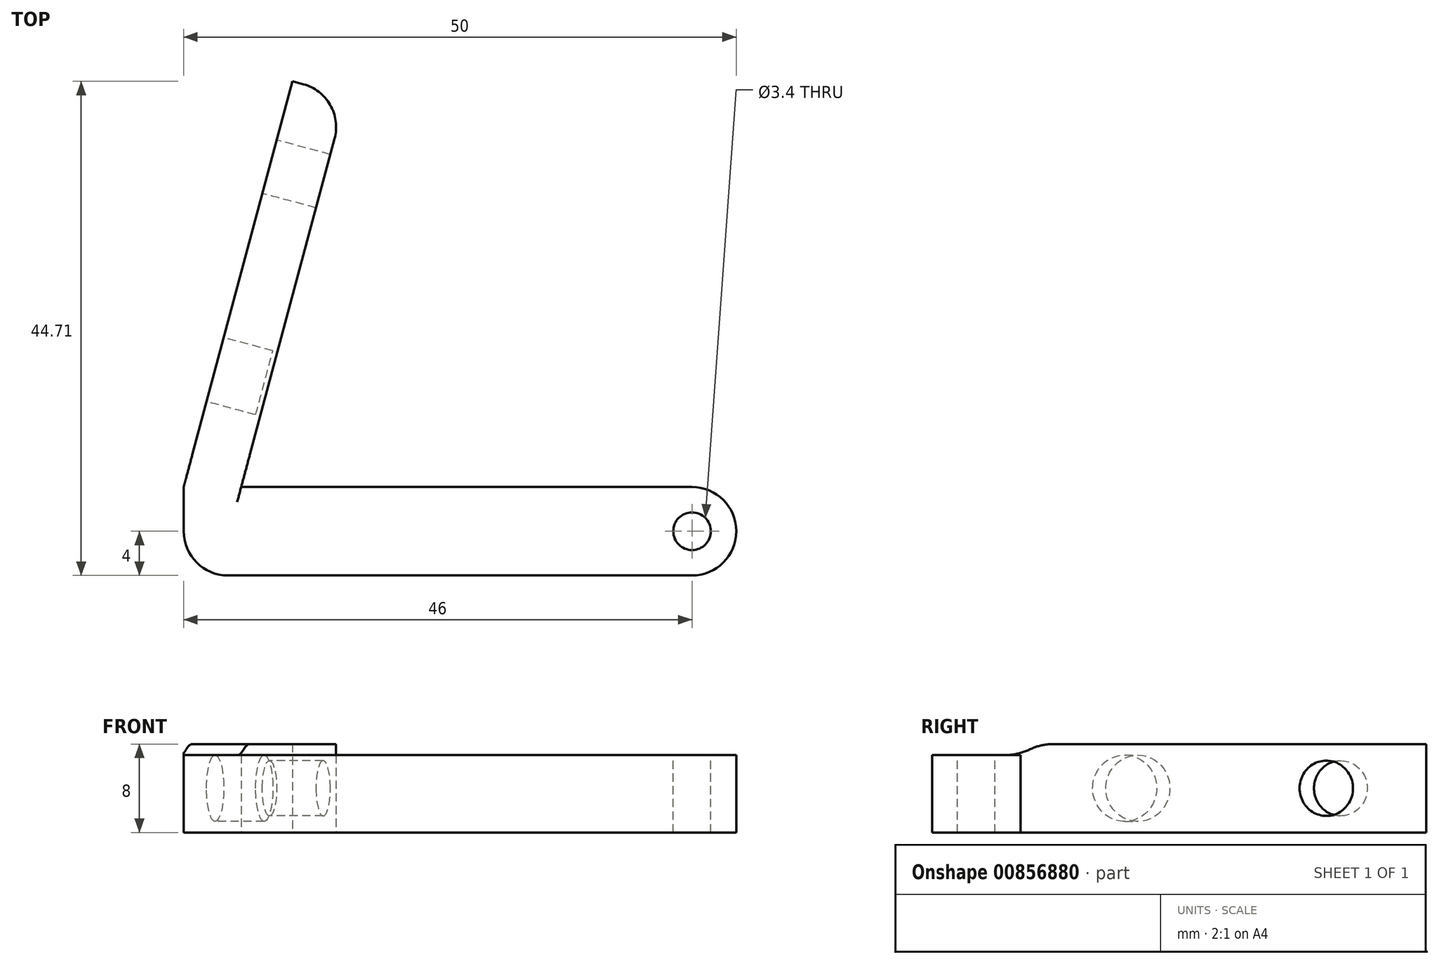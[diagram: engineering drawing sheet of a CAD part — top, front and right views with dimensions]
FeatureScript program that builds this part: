
annotation { "Feature Type Name" : "Feature", "Feature Type Description" : "" }
export const myFeature = defineFeature(function(context is Context, id is Id, definition is map)
    precondition{}
    {
        {
            var Q0;
            Q0=qCreatedBy(makeId("Top.planeOp"),FACE);
            var sketch = newSketch(context, id + "F0", { "sketchPlane" : qUnion([Q0])});
            skLineSegment(sketch, "E0.bottom", {"start": v(25, -4) * mm, "end": v(-25, -4) * mm});
            skLineSegment(sketch, "E0.top", {"start": v(25, 4) * mm, "end": v(-25, 4) * mm});
            skLineSegment(sketch, "E0.left", {"start": v(25, -4) * mm, "end": v(25, 4) * mm});
            skLineSegment(sketch, "E0.right", {"start": v(-25, -4) * mm, "end": v(-25, 4) * mm});
            skPoint(sketch, "E0.middle", {"position": v(0, 0) * mm});
            skLineSegment(sketch, "E1", {"start": v(-25, 4) * mm, "end": v(-15.16, 40.7) * mm});
            skLineSegment(sketch, "E2", {"start": v(-15.16, 40.7) * mm, "end": v(-10.31, 39.4) * mm});
            skLineSegment(sketch, "E3", {"start": v(-10.31, 39.4) * mm, "end": v(-19.8, 4) * mm});
            skSolve(sketch);
        }
        {
            var Q0;
            Q0=makeQuery(id+"F0.imprint","IMPRINT",FACE,{"disambiguationData":[TD([[makeQuery(id+"F0.imprint","IMPRINT",EDGE,{"derivedFrom":sQuery(id+"F0.wireOp",EDGE,"E0.bottom")}),-1.0]])]});
            extrude(context, id + "F1", {"entities" : qUnion([Q0]), "depth" : 7 * mm, "offsetDistance" : 25 * mm});
        }
        {
            var Q0;
            {var subQ0=sQuery(id+"F0.wireOp",EDGE,"E1");Q0=makeQuery(id+"F0.imprint","IMPRINT",FACE,{"disambiguationData":[TD([[makeQuery(id+"F0.imprint","IMPRINT",EDGE,{"derivedFrom":subQ0}),-1.0]])]});}
            extrude(context, id + "F2", {"entities" : qUnion([Q0]), "operationType" : NewBodyOperationType.ADD, "depth" : 8 * mm, "offsetDistance" : 25 * mm});
        }
        {
            var Q0;
            Q0=makeQuery(id+"F1.opExtrude","SWEPT_EDGE",EDGE,{"disambiguationData":[OSD([sQuery(id+"F0.wireOp",EDGE,"E0.top"),sQuery(id+"F0.wireOp",EDGE,"E0.left")])]});
            var Q1;
            Q1=makeQuery(id+"F1.opExtrude","SWEPT_EDGE",EDGE,{"disambiguationData":[OSD([sQuery(id+"F0.wireOp",EDGE,"E0.bottom"),sQuery(id+"F0.wireOp",EDGE,"E0.left")])]});
            var Q2;
            Q2=makeQuery(id+"F1.opExtrude","SWEPT_EDGE",EDGE,{"disambiguationData":[OSD([sQuery(id+"F0.wireOp",EDGE,"E0.bottom"),sQuery(id+"F0.wireOp",EDGE,"E0.right")])]});
            var Q3;
            Q3=makeQuery(id+"F2.opExtrude","SWEPT_EDGE",EDGE,{"disambiguationData":[OSD([sQuery(id+"F0.wireOp",EDGE,"E2"),sQuery(id+"F0.wireOp",EDGE,"E3")])]});
            fillet(context, id + "F3", {"entities" : qUnion([Q0, Q1, Q2, Q3]), "radius" : 4 * mm, "tangentPropagation" : true, "allowEdgeOverflow" : false});
        }
        {
            var Q0;
            Q0=makeQuery(id+"F2.opExtrude","CAP_EDGE",EDGE,{"disambiguationData":[OSD([sQuery(id+"F0.wireOp",EDGE,"E0.top")])],"isStart":false});
            fillet(context, id + "F4", {"entities" : qUnion([Q0]), "radius" : 5 * mm, "tangentPropagation" : true, "allowEdgeOverflow" : false});
        }
        {
            var Q0;
            {var subQ0=sQuery(id+"F0.wireOp",EDGE,"E0.top");Q0=makeQuery(id+"F4.opFillet","BLEND_EDGE",EDGE,{"blendedFrom":[makeQuery(id+"F2.opExtrude","CAP_EDGE",EDGE,{"disambiguationData":[OSD([subQ0])],"isStart":false}),makeQuery(id+"F1.opExtrude","CAP_FACE",FACE,{"disambiguationData":[OSD([sQuery(id+"F0.wireOp",EDGE,"E0.bottom"),subQ0,sQuery(id+"F0.wireOp",EDGE,"E0.left"),sQuery(id+"F0.wireOp",EDGE,"E0.right")])],"isStart":false})],"blendedInto":[makeQuery(id+"F1.opExtrude","CAP_FACE",FACE,{"disambiguationData":[OSD([sQuery(id+"F0.wireOp",EDGE,"E0.bottom"),subQ0,sQuery(id+"F0.wireOp",EDGE,"E0.left"),sQuery(id+"F0.wireOp",EDGE,"E0.right")])],"isStart":false})]});}
            fillet(context, id + "F5", {"entities" : qUnion([Q0]), "radius" : 5 * mm, "tangentPropagation" : true, "allowEdgeOverflow" : false});
        }
        {
            var Q0;
            Q0=makeQuery(id+"F2.opExtrude","SWEPT_FACE",FACE,{"disambiguationData":[OSD([sQuery(id+"F0.wireOp",EDGE,"E1")])]});
            var sketch = newSketch(context, id + "F6", { "sketchPlane" : qUnion([Q0])});
            skCircle(sketch, "E4", {"center": v(-27.4, 4) * mm, "radius": 2.5 * mm});
            skPoint(sketch, "E4.centerSnap0", {"position": v(-35.4, 4) * mm});
            skCircle(sketch, "E5", {"center": v(-8.4, 4) * mm, "radius": 3 * mm});
            skSolve(sketch);
        }
        {
            var Q0;
            Q0=makeQuery(id+"F6.imprint","IMPRINT",FACE,{"disambiguationData":[TD([[makeQuery(id+"F6.imprint","IMPRINT",EDGE,{"derivedFrom":sQuery(id+"F6.wireOp",EDGE,"E4")}),1.0]])]});
            extrude(context, id + "F7", {"entities" : qUnion([Q0]), "operationType" : NewBodyOperationType.REMOVE, "oppositeDirection" : true, "depth" : 10 * mm, "offsetDistance" : 25 * mm});
        }
        {
            var Q0;
            Q0=makeQuery(id+"F6.imprint","IMPRINT",FACE,{"disambiguationData":[TD([[makeQuery(id+"F6.imprint","IMPRINT",EDGE,{"derivedFrom":sQuery(id+"F6.wireOp",EDGE,"E5")}),1.0]])]});
            extrude(context, id + "F8", {"entities" : qUnion([Q0]), "operationType" : NewBodyOperationType.REMOVE, "oppositeDirection" : true, "depth" : 4.6 * mm, "offsetDistance" : 25 * mm});
        }
        {
            var Q0;
            Q0=makeQuery(id+"F1.opExtrude","CAP_FACE",FACE,{"disambiguationData":[OSD([sQuery(id+"F0.wireOp",EDGE,"E0.bottom"),sQuery(id+"F0.wireOp",EDGE,"E0.top"),sQuery(id+"F0.wireOp",EDGE,"E0.left"),sQuery(id+"F0.wireOp",EDGE,"E0.right")])],"isStart":false});
            var sketch = newSketch(context, id + "F9", { "sketchPlane" : qUnion([Q0])});
            skCircle(sketch, "E6", {"center": v(21, 0) * mm, "radius": 1.7 * mm});
            skSolve(sketch);
        }
        {
            var Q0;
            Q0=makeQuery(id+"F9.imprint","IMPRINT",FACE,{"disambiguationData":[TD([[makeQuery(id+"F9.imprint","IMPRINT",EDGE,{"derivedFrom":sQuery(id+"F9.wireOp",EDGE,"E6")}),1.0]])]});
            extrude(context, id + "F10", {"entities" : qUnion([Q0]), "operationType" : NewBodyOperationType.REMOVE, "endBound" : BoundingType.THROUGH_ALL, "oppositeDirection" : true, "depth" : 25 * mm, "offsetDistance" : 25 * mm});
        }
    });
